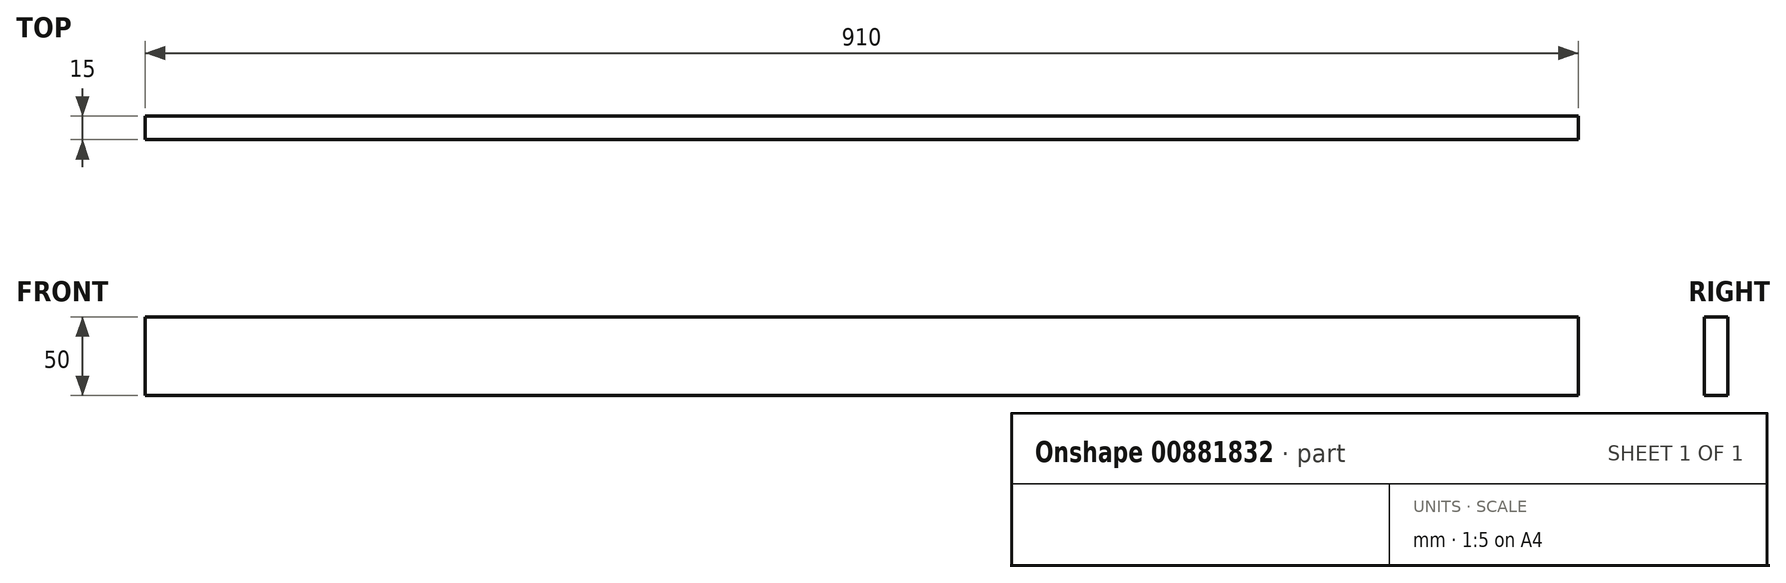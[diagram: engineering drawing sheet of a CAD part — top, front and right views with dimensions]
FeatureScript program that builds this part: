
annotation { "Feature Type Name" : "Feature", "Feature Type Description" : "" }
export const myFeature = defineFeature(function(context is Context, id is Id, definition is map)
    precondition{}
    {
        {
            var Q0;
            Q0=qCreatedBy(makeId("Front.planeOp"),FACE);
            var sketch = newSketch(context, id + "F0", { "sketchPlane" : qUnion([Q0])});
            skLineSegment(sketch, "E0", {"start": v(-48.8, 25.89) * mm, "end": v(861.2, 25.89) * mm});
            skLineSegment(sketch, "E1", {"start": v(861.2, 75.89) * mm, "end": v(-48.8, 75.89) * mm});
            skLineSegment(sketch, "E2", {"start": v(-48.8, 75.89) * mm, "end": v(-48.8, 25.89) * mm});
            skLineSegment(sketch, "E3", {"start": v(861.2, 25.89) * mm, "end": v(861.2, 75.89) * mm});
            skSolve(sketch);
        }
        {
            var Q0;
            Q0 = qSketchRegion(id + "F0", true);
            extrude(context, id + "F1", {"entities" : qUnion([Q0]), "depth" : 15 * mm, "offsetDistance" : 25 * mm});
        }
    });
